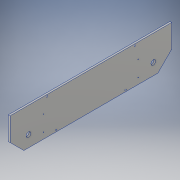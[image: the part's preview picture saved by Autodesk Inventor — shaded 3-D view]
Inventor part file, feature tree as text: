
AUTODESK INVENTOR PART (.ipt)
format: ipt  version: 2019 (Build 230136000, 136)  size: 154,624 bytes
history: native  units: in
note: dims shown in document units (in); Inventor stores cm internally (conversion verified against a paired STEP export)
features: sketch x3, chamfer x2, hole x2, extrude x1, projected_geometry x1
ambient origin geometry x8: Origin, YZ Plane, XZ Plane, XY Plane, X Axis, Y Axis, Z Axis, Center Point
bodies: Solid1 (feature_tree)
feature tree (9):
  extrude  "Extrusion1"  Depth=17.5in
  chamfer  "Chamfer1"  Distance=2.0in
  chamfer  "Chamfer2"  Distance=2.0in
  hole  "Hole2"  [1 undecoded]
  hole  "Hole3"  [1 undecoded]
  sketch  "Sketch1"  dims[d0=4.0in d1=17.5in]
  sketch  "Sketch7"  dims[d2=0.501in]
  projected_geometry  "Projected Loop6"
  sketch  "Sketch9"  dims[d3=1.25in d4=2.0in d5=2.0in d6=0.1875in d7=0.0in d8=1.5in d9=0.125in d10=45.0deg d11=1.5in d12=0.125in d13=45.0deg d22=6.517in d23=0.125in d24=0.603in d25=0.125in d26=0.63in d27=6.517in d28=0.125in d29=0.603in d30=6.517in d31=0.125in d32=0.63in d33=6.517in d95=0.175in d96=0.175in d97=0.175in d98=0.175in d99=4.0in d100=4.0in d101=5.0in d102=5.0in d103=0.15in d104=0.75in d105=0.375in d106=0.25in d107=0.5635in d108=1.0in d109=0.8108in d115=1.7in d116=3.625in d117=3.625in d118=0.65in d119=3.625in d120=3.625in d121=1.7in d122=0.65in d123=0.08in d124=0.198in d125=0.375in d126=0.25in d127=0.5635in d128=0.302in d129=0.8108in]
note: 2 required parameter values undecoded (feature->parameter linkage not recoverable at this tier; creation-order binding heuristic only, values carry confidence <= 0.55)
